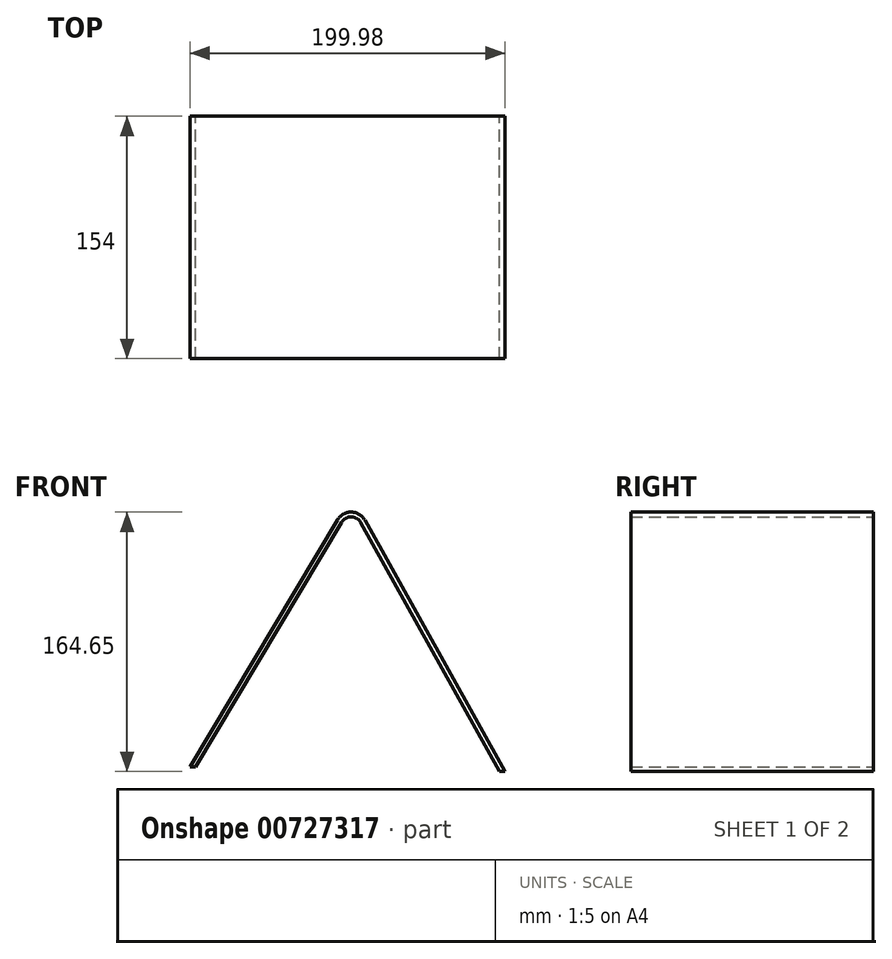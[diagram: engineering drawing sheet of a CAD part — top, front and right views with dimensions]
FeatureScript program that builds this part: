
annotation { "Feature Type Name" : "Feature", "Feature Type Description" : "" }
export const myFeature = defineFeature(function(context is Context, id is Id, definition is map)
    precondition{}
    {
        {
            var Q0;
            Q0=qCreatedBy(makeId("Front.planeOp"),FACE);
            var sketch = newSketch(context, id + "F0", { "sketchPlane" : qUnion([Q0])});
            skLineSegment(sketch, "E0.0", {"start": v(29, 192.45) * mm, "end": v(118.03, 32.93) * mm});
            skLineSegment(sketch, "E0.1", {"start": v(118.03, 32.93) * mm, "end": v(114.57, 32.98) * mm});
            skLineSegment(sketch, "E0.2", {"start": v(-81.95, 35.85) * mm, "end": v(11.69, 192.7) * mm});
            skPoint(sketch, "E0.0.midPoint", {"position": v(49.34, -62.67) * mm});
            skPoint(sketch, "E1.visualSharp", {"position": v(20.57, 207.57) * mm});
            skArc(sketch, "E1.filletArc", {"start": v(29, 192.45) * mm, "mid": v(20.42, 197.58) * mm, "end": v(11.69, 192.7) * mm});
            skLineSegment(sketch, "E2.0", {"start": v(26.39, 190.99) * mm, "end": v(114.57, 32.98) * mm});
            skArc(sketch, "E2.1", {"start": v(26.39, 190.99) * mm, "mid": v(20.38, 194.58) * mm, "end": v(14.27, 191.16) * mm});
            skLineSegment(sketch, "E2.2", {"start": v(-78.48, 35.8) * mm, "end": v(14.27, 191.16) * mm});
            skLineSegment(sketch, "E3.trimOffspring", {"start": v(-78.48, 35.8) * mm, "end": v(-81.95, 35.85) * mm});
            skSolve(sketch);
        }
        {
            var Q0;
            Q0=makeQuery(id+"F0.imprint","IMPRINT",FACE,{"disambiguationData":[TD([[makeQuery(id+"F0.imprint","IMPRINT",EDGE,{"derivedFrom":sQuery(id+"F0.wireOp",EDGE,"E0.0")}),-1.0]])]});
            extrude(context, id + "F1", {"entities" : qUnion([Q0]), "depth" : 154 * mm});
        }
    });
